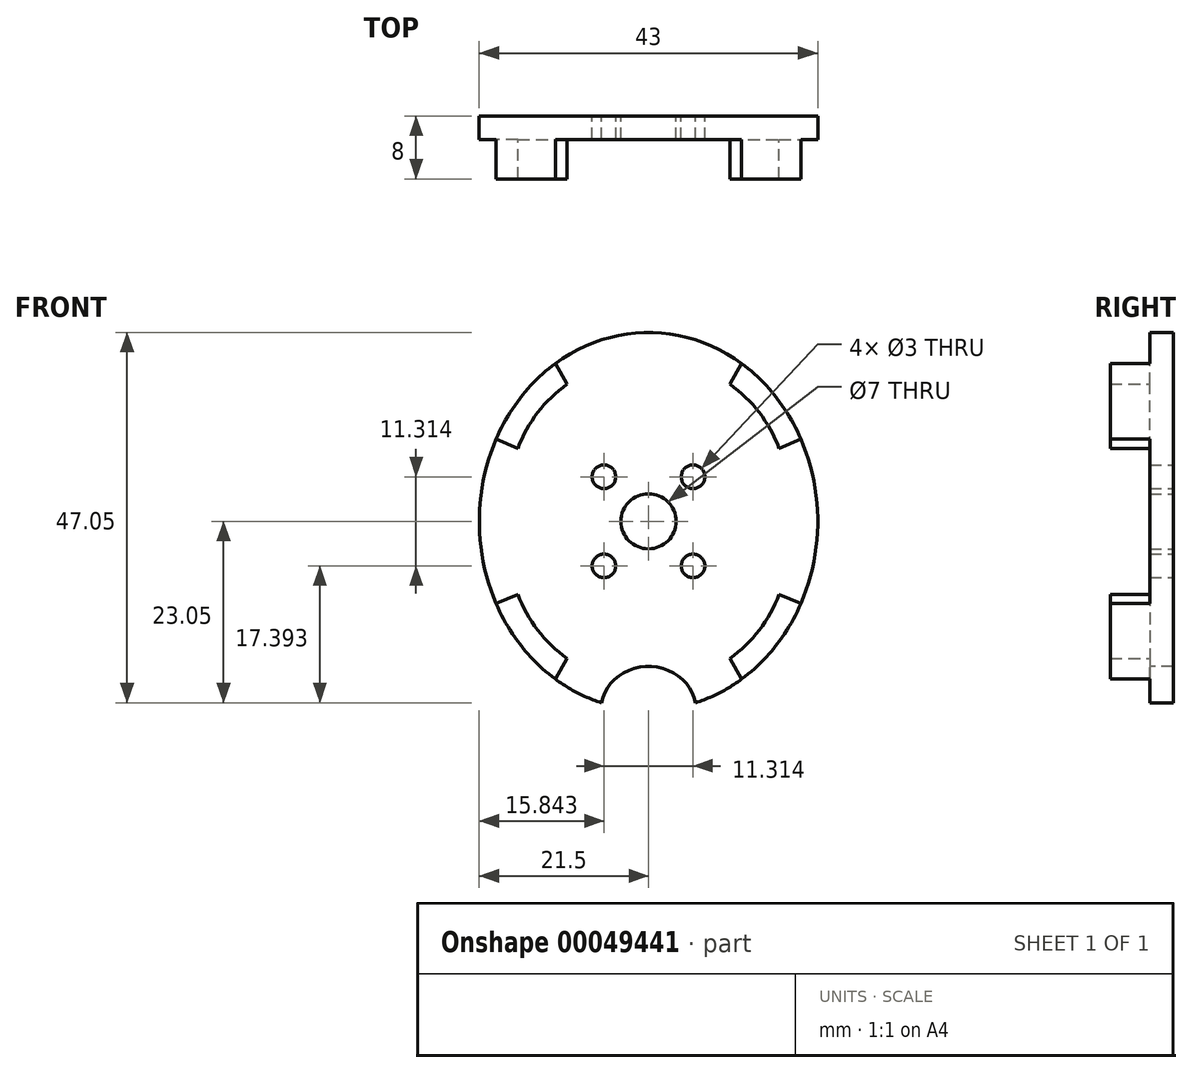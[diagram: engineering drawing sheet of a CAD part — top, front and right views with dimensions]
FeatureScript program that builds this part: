
annotation { "Feature Type Name" : "Feature", "Feature Type Description" : "" }
export const myFeature = defineFeature(function(context is Context, id is Id, definition is map)
    precondition{}
    {
        {
            var Q0;
            Q0=qCreatedBy(makeId("Front.planeOp"),FACE);
            var sketch = newSketch(context, id + "F0", { "sketchPlane" : qUnion([Q0])});
            skEllipticalArc(sketch, "E0", {});
            skCircle(sketch, "E1", {"center": v(0, 0) * mm, "radius": 8 * mm, "construction": true});
            skLineSegment(sketch, "E2", {"start": v(0, 0) * mm, "end": v(5.66, 5.66) * mm, "construction": true});
            skCircle(sketch, "E3", {"center": v(5.66, 5.66) * mm, "radius": 1.5 * mm});
            skCircle(sketch, "E4.1.0", {"center": v(5.66, -5.66) * mm, "radius": 1.5 * mm});
            skCircle(sketch, "E4.2.0", {"center": v(-5.66, -5.66) * mm, "radius": 1.5 * mm});
            skCircle(sketch, "E4.3.0", {"center": v(-5.66, 5.66) * mm, "radius": 1.5 * mm});
            skLineSegment(sketch, "E4.anchor2", {"start": v(0, 0) * mm, "end": v(-5.66, 5.66) * mm, "construction": true});
            skEllipticalArc(sketch, "E5", {});
            skPoint(sketch, "E6.orphan", {"position": v(0, -18.62) * mm});
            skCircle(sketch, "E7", {"center": v(0, 0) * mm, "radius": 3.5 * mm});
            const initialGuessF0  = {"E0": [0, 0, 0, 1, 0.024, 0.0215, 3.423189095404466, 2.859996211775119], "E5": [0, -0.024, -1, 0, 0.00606221443115755, 0.005581033474772104, 3.3117880856813957, 6.112989875087983]};
            skSetInitialGuess(sketch, initialGuessF0);
            skSolve(sketch);
        }
        {
            var Q0;
            Q0=makeQuery(id+"F0.imprint","IMPRINT",FACE,{"disambiguationData":[TD([[makeQuery(id+"F0.imprint","IMPRINT",EDGE,{"derivedFrom":sQuery(id+"F0.wireOp",EDGE,"E0")}),1.0]])]});
            extrude(context, id + "F1", {"entities" : qUnion([Q0]), "depth" : 3 * mm});
        }
        {
            var Q0;
            Q0=makeQuery(id+"F1.opExtrude","CAP_FACE",FACE,{"disambiguationData":[OSD([sQuery(id+"F0.wireOp",EDGE,"E0"),sQuery(id+"F0.wireOp",EDGE,"E3"),sQuery(id+"F0.wireOp",EDGE,"E4.1.0"),sQuery(id+"F0.wireOp",EDGE,"E4.2.0"),sQuery(id+"F0.wireOp",EDGE,"E4.3.0"),sQuery(id+"F0.wireOp",EDGE,"E5")])],"isStart":false});
            var sketch = newSketch(context, id + "F2", { "sketchPlane" : qUnion([Q0])});
            skLineSegment(sketch, "E8", {"start": v(0, 0) * mm, "end": v(16.01, 16.01) * mm, "construction": true});
            skEllipticalArc(sketch, "E9", {});
            skLineSegment(sketch, "E10", {"start": v(16.6, 9.28) * mm, "end": v(19.36, 10.45) * mm});
            skLineSegment(sketch, "E11", {"start": v(10.33, 17.41) * mm, "end": v(11.83, 20.04) * mm});
            skLineSegment(sketch, "E12.MirrorCS", {"start": v(10.33, -17.41) * mm, "end": v(11.83, -20.04) * mm});
            skEllipticalArc(sketch, "E13.MirrorCS", {});
            skLineSegment(sketch, "E14.MirrorCS", {"start": v(16.6, -9.28) * mm, "end": v(19.36, -10.45) * mm});
            skLineSegment(sketch, "E15.MirrorCS", {"start": v(-10.33, 17.41) * mm, "end": v(-11.83, 20.04) * mm});
            skEllipticalArc(sketch, "E16.MirrorCS", {});
            skLineSegment(sketch, "E17.MirrorCS", {"start": v(-16.6, 9.28) * mm, "end": v(-19.36, 10.45) * mm});
            skArc(sketch, "E18", {"start": v(16.6, 9.28) * mm, "mid": v(14.07, 13.81) * mm, "end": v(10.33, 17.41) * mm});
            skArc(sketch, "E19.MirrorCS", {"start": v(-16.6, 9.28) * mm, "mid": v(-14.07, 13.81) * mm, "end": v(-10.33, 17.41) * mm});
            skArc(sketch, "E20.MirrorCS", {"start": v(16.6, -9.28) * mm, "mid": v(14.07, -13.81) * mm, "end": v(10.33, -17.41) * mm});
            skLineSegment(sketch, "E21.MirrorCS", {"start": v(-16.6, -9.28) * mm, "end": v(-19.36, -10.45) * mm});
            skEllipticalArc(sketch, "E22.MirrorCS", {});
            skArc(sketch, "E23.MirrorCS", {"start": v(-16.6, -9.28) * mm, "mid": v(-14.07, -13.81) * mm, "end": v(-10.33, -17.41) * mm});
            skLineSegment(sketch, "E24.MirrorCS", {"start": v(-10.33, -17.41) * mm, "end": v(-11.83, -20.04) * mm});
            const initialGuessF2  = {"E9": [0, 0, 1, 0, 0.0215, 0.024, 0.45031396467637297, 0.9883681275279574], "E13.MirrorCS": [0, 0, 1, 0, 0.0215, 0.024, 5.294817179651629, 5.832871342503212], "E16.MirrorCS": [0, 0, -1, 0, 0.0215, 0.024, 5.294817179651629, 5.832871342503213], "E22.MirrorCS": [0, 0, -1, 0, 0.0215, 0.024, 0.45031396467637386, 0.9883681275279574]};
            skSetInitialGuess(sketch, initialGuessF2);
            skSolve(sketch);
        }
        {
            var Q0;
            Q0 = qSketchRegion(id + "F2", true);
            extrude(context, id + "F3", {"entities" : qUnion([Q0]), "operationType" : NewBodyOperationType.ADD, "depth" : 5 * mm});
        }
    });
